# Revit family: Proto_Room_Tag
name_source: partatom
category: Room Tags
revit_build: Autodesk Revit 2016 (Build: 20170117_1200(x64)
units: mm (PartAtom-declared; Revit-internal decimal feet)

## types (8) — shared parameters

## per-type parameters (varying)
| type | Show Area | Show Room Number | Show Signage Info | Show Volume | Standard Room Name |
| Presentation | No | No | No | No | No |
| Presentation with Area | Yes | No | No | No | No |
| Standard with Volume | No | Yes | No | Yes | Yes |
| Proto Standard with Area | Yes | Yes | No | No | Yes |
| Proto Standard | No | Yes | No | No | Yes |
| Signage | No | No | Yes | No | No |
| Signage with Area | Yes | No | Yes | No | No |
| Standard L x W | No | Yes | No | No | Yes |

type visibility flags (boolean, named after types; folded from table):
- Presentation: Yes: Presentation Room Name
- Presentation with Area: Yes: Presentation Room Name
- Standard with Volume: Yes: (none)
- Proto Standard with Area: Yes: (none)
- Proto Standard: Yes: (none)
- Signage: Yes: (none)
- Signage with Area: Yes: (none)
- Standard L x W: Yes: (none)
